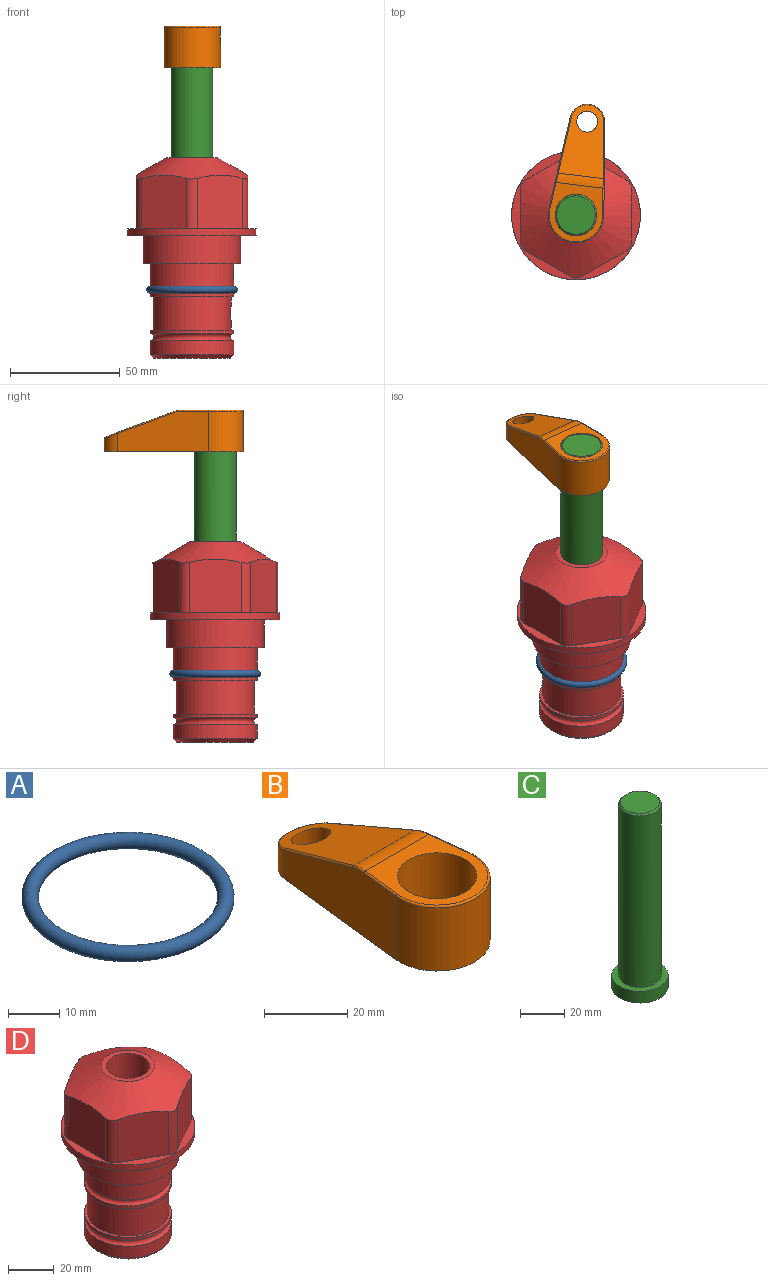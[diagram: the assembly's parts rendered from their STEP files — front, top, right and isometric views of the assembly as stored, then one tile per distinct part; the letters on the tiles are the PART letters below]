
ASSEMBLY  parts=4 mates=2
PART A: 1 faces, bbox 44.7x44.7x3.2 mm
  f0: torus R=19.05mm, axis (0,0,1), area 1193.9mm2
PART B: 44 faces, bbox 27.5x64.5x19.1 mm
  f0: plane 2.3x0.95mm, normal (0,0,-1), area 1mm2, adj f25,f30,f34
  f1: plane 63.5x25.4mm, normal (0,0,-1), area 561.7mm2, adj f2,f3,f4,f5,f6,f7,f19,f20
  f2: cylinder r=12.7mm len=25.4mm, axis (0,0,-1), area 792.2mm2, adj f1,f3,f5,f13
  f3: plane 42.33x18.54mm, normal (0.99,0.11,0), area 647mm2, adj f1,f2,f4,f11,f12,f14
  f4: cylinder r=7.94mm len=15.78mm, axis (0,0,-1), area 158.6mm2, adj f1,f3,f5,f16
  f5: plane 42.33x18.54mm, normal (-0.99,0.11,0), area 647mm2, adj f1,f2,f4,f15,f17,f18
  f6: cylinder r=9.53mm len=19.05mm, axis (0,0,-1), area 1140.1mm2, adj f1,f8
  f7: cylinder r=4.76mm len=10.98mm, axis (0,0,-1), area 276.1mm2, adj f1,f9
  f8: plane 25.83x24.38mm, normal (0,0,1), area 262.2mm2, adj f6,f10,f11,f13,f15
  f9: plane 32.49x20.55mm, normal (0,0.34,0.94), area 489.9mm2, adj f7,f10,f14,f16,f18
  f10: cylinder r=12.7mm len=21.49mm, axis (-1,0,0), area 93.2mm2, adj f8,f9,f12,f17
  f11: cylinder r=0.51mm len=12.34mm, axis (0.11,-0.99,0), area 9.9mm2, adj f3,f8,f12,f13
  f12: bspline ~7.62x1.64mm, area 3.5mm2, adj f3,f10,f11,f14
  f13: torus R=12.19mm, axis (0,0,1), area 33.6mm2, adj f2,f8,f11,f15
  f14: cylinder r=0.51mm len=26.01mm, axis (0.1,-0.93,0.34), area 21.6mm2, adj f3,f9,f12,f16
  f15: cylinder r=0.51mm len=12.34mm, axis (0.11,0.99,0), area 9.9mm2, adj f5,f8,f13,f17
  f16: bspline ~15.78x7.05mm, area 15.7mm2, adj f4,f9,f14,f18
  f17: bspline ~7.62x1.64mm, area 3.5mm2, adj f5,f10,f15,f18
  f18: cylinder r=0.51mm len=26.01mm, axis (0.1,0.93,-0.34), area 21.6mm2, adj f5,f9,f16,f17
  f19: plane 21.6x14.29mm, normal (-0.99,-0.11,0), area 242.6mm2, adj f1,f26,f28,f34,f36,f38
  f20: plane 21.6x14.29mm, normal (0.99,-0.11,0), area 242.6mm2, adj f1,f27,f29,f37,f39,f41
  f21: cylinder r=12.7mm len=14.29mm, axis (0,0,-1), area 173.2mm2, adj f1,f26,f27,f30,f31,f33
  f22: cylinder r=7.94mm len=7.63mm, axis (0,0,-1), area 53.8mm2, adj f1,f28,f29,f42
  f23: plane 2.3x0.95mm, normal (0,0,-1), area 1mm2, adj f25,f33,f37
  f24: plane 17.94x12.32mm, normal (0,-0.34,-0.94), area 191.2mm2, adj f25,f38,f41,f42
  f25: cylinder r=9.53mm len=12.93mm, axis (-1,0,0), area 37.5mm2, adj f0,f23,f24,f31,f36,f39
  f26: cylinder r=1.59mm len=14.29mm, axis (0,0,-1), area 49mm2, adj f1,f19,f21,f32
  f27: cylinder r=1.59mm len=14.29mm, axis (0,0,-1), area 49mm2, adj f1,f20,f21,f35
  f28: cylinder r=1.59mm len=7.28mm, axis (0,0,-1), area 22.1mm2, adj f1,f19,f22,f40
  f29: cylinder r=1.59mm len=7.28mm, axis (0,0,-1), area 22.1mm2, adj f1,f20,f22,f43
  f30: torus R=14.29mm, axis (0,0,1), area 5.8mm2, adj f0,f21,f31,f32
  f31: bspline ~11.06x2.73mm, area 20.8mm2, adj f21,f25,f30,f33
  f32: sphere r=1.59mm, area 5.4mm2, adj f26,f30,f34
  f33: torus R=14.29mm, axis (0,0,1), area 5.8mm2, adj f21,f23,f31,f35
  f34: cylinder r=1.59mm len=1.68mm, axis (-0.11,0.99,0), area 2.4mm2, adj f0,f19,f32,f36
  f35: sphere r=1.59mm, area 5.4mm2, adj f27,f33,f37
  f36: bspline ~5.82x2.33mm, area 7.7mm2, adj f19,f25,f34,f38
  f37: cylinder r=1.59mm len=1.68mm, axis (0.11,0.99,0), area 2.4mm2, adj f20,f23,f35,f39
  f38: cylinder r=1.59mm len=18.33mm, axis (0.1,-0.93,0.34), area 46.7mm2, adj f19,f24,f36,f40
  f39: bspline ~5.82x2.33mm, area 7.7mm2, adj f20,f25,f37,f41
  f40: sphere r=1.59mm, area 3.6mm2, adj f28,f38,f42
  f41: cylinder r=1.59mm len=18.33mm, axis (0.1,0.93,-0.34), area 46.7mm2, adj f20,f24,f39,f43
  f42: bspline ~8.31x1.84mm, area 15.3mm2, adj f22,f24,f40,f43
  f43: sphere r=1.59mm, area 3.6mm2, adj f29,f41,f42
PART C: 6 faces, bbox 25.4x25.4x101.6 mm
  f0: plane 17.46x17.46mm, normal (0,0,1), area 239.5mm2, adj f5
  f1: plane 25.4x25.4mm, normal (0,0,-1), area 506.7mm2, adj f2
  f2: cylinder r=12.7mm len=25.4mm, axis (0,0,1), area 506.7mm2, adj f1,f3
  f3: plane 25.4x25.4mm, normal (0,0,1), area 221.7mm2, adj f2,f4
  f4: cylinder r=9.53mm len=94.46mm, axis (0,0,1), area 5653mm2, adj f3,f5
  f5: cone r=8.73mm half-angle=45deg, axis (0,0,-1), area 64.4mm2, adj f0,f4
PART D: 36 faces, bbox 58.7x58.7x91.2 mm
  f0: cylinder r=17.78mm len=35.56mm, axis (0,0,1), area 1670.8mm2, adj f23,f24,f31
  f1: cylinder r=19.05mm len=38.1mm, axis (0,0,1), area 1191.9mm2, adj f26,f27,f30
  f2: plane 58.66x58.66mm, normal (0,0,-1), area 1150.6mm2, adj f3,f28
  f3: cylinder r=29.33mm len=58.66mm, axis (0,0,-1), area 585.1mm2, adj f2,f4
  f4: plane 58.66x58.66mm, normal (0,0,1), area 475.9mm2, adj f3,f5,f6,f7,f8,f9,f10,f11
  f5: plane 24.5x20.32mm, normal (-0.5,0.87,0), area 562.8mm2, adj f4,f15,f16,f17
  f6: plane 24.5x20.32mm, normal (0.5,0.87,0), area 562.8mm2, adj f4,f14,f15,f17
  f7: plane 24.5x23.48mm, normal (1,0,0), area 562.8mm2, adj f4,f13,f14,f17
  f8: plane 24.5x20.32mm, normal (0.5,-0.87,0), area 562.8mm2, adj f4,f12,f13,f17
  f9: plane 24.5x20.32mm, normal (-0.5,-0.87,0), area 562.8mm2, adj f4,f11,f12,f17
  f10: plane 24.5x23.48mm, normal (-1,0,0), area 562.8mm2, adj f4,f11,f16,f17
  f11: cylinder r=5.08mm len=23.01mm, axis (0,0,-1), area 121.2mm2, adj f4,f9,f10,f17
  f12: cylinder r=5.08mm len=23.01mm, axis (0,0,-1), area 121.2mm2, adj f4,f8,f9,f17
  f13: cylinder r=5.08mm len=23.01mm, axis (0,0,-1), area 121.2mm2, adj f4,f7,f8,f17
  f14: cylinder r=5.08mm len=23.01mm, axis (0,0,-1), area 121.2mm2, adj f4,f6,f7,f17
  f15: cylinder r=5.08mm len=23.01mm, axis (0,0,-1), area 121.2mm2, adj f4,f5,f6,f17
  f16: cylinder r=5.08mm len=23.01mm, axis (0,0,-1), area 121.2mm2, adj f4,f5,f10,f17
  f17: cone r=11.73mm half-angle=60deg, axis (0,0,-1), area 2071.8mm2, adj f5,f6,f7,f8,f9,f10,f11,f12
  f18: plane 23.46x23.46mm, normal (0,0,1), area 147.4mm2, adj f17,f35
  f19: plane 34.93x34.93mm, normal (0,0,-1), area 958mm2, adj f29
  f20: cylinder r=19.05mm len=38.1mm, axis (0,0,1), area 760.1mm2, adj f21,f29
  f21: torus R=19.05mm, axis (0,0,1), area 565.3mm2, adj f20,f22
  f22: cylinder r=19.05mm len=38.1mm, axis (0,0,1), area 190mm2, adj f21,f23
  f23: plane 38.1x38.1mm, normal (0,0,1), area 146.9mm2, adj f0,f22
  f24: plane 38.1x38.1mm, normal (0,0,-1), area 146.9mm2, adj f0,f25
  f25: cylinder r=19.05mm len=38.1mm, axis (0,0,1), area 190mm2, adj f24,f26
  f26: torus R=19.05mm, axis (0,0,1), area 565.3mm2, adj f1,f25
  f27: plane 44.45x44.45mm, normal (0,0,-1), area 411.7mm2, adj f1,f28
  f28: cylinder r=22.23mm len=44.45mm, axis (0,0,1), area 1773.5mm2, adj f2,f27
  f29: cone r=19.05mm half-angle=45deg, axis (0,0,1), area 257.5mm2, adj f19,f20
  f30: cylinder r=3.17mm len=6.75mm, axis (-1,0,0), area 128mm2, adj f1,f33
  f31: cylinder r=3.17mm len=6.35mm, axis (-1,0,0), area 102.5mm2, adj f0,f33
  f32: plane 25.4x25.4mm, normal (0,0,1), area 506.7mm2, adj f33
  f33: cylinder r=12.7mm len=66.42mm, axis (0,0,-1), area 5236.2mm2, adj f30,f31,f32,f34
  f34: cone r=9.53mm half-angle=30deg, axis (0,0,-1), area 443.4mm2, adj f33,f35
  f35: cylinder r=9.53mm len=19.05mm, axis (0,0,-1), area 849mm2, adj f18,f34
PLACE A at identity
PLACE B rot(axis=(0,0,-1),6.8deg) t=(0,0,76.5)mm
PLACE C rot(axis=(0,0,-1),96.8deg) t=(0,0,21.89)mm
PLACE D at identity fixed
MATE fastened B.f2 <-> C.f2  axis (0,0,-1) through (0,0,95.55)mm
MATE cylindrical C.f2 <-> D.f0  axis (0,0,1) through (0,0,47.53)mm
